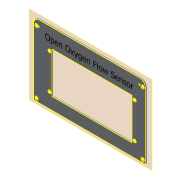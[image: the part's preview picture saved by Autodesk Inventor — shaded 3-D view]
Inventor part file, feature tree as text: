
AUTODESK INVENTOR PART (.ipt)
format: ipt  version: 2019.4 (Build 234330000, 330)  size: 126,976 bytes
history: native  units: mm
features: sketch x2, other x2, plane x1, extrude x1, fillet x1, reference x1, projected_geometry x1
ambient origin geometry x8: Origin, YZ Plane, XZ Plane, XY Plane, X Axis, Y Axis, Z Axis, Center Point
bodies: Solid1 (feature_tree)
feature tree (9):
  plane  "Work Plane1"
  extrude  "Extrusion1"  Depth=36.0mm
  fillet  "Fillet1"  Radius=74.5mm
  sketch  "Sketch2"  dims[d3=31.0mm d4=2.8mm d5=2.8mm d6=2.8mm d7=2.8mm d8=1.0mm d9=0.0mm d10=5.0mm]
  sketch  "Sketch1"  dims[d0=70.0mm d1=36.0mm d2=74.5mm]
  reference  "Reference1"
  projected_geometry  "Projected Loop1"
  other  "Assemlby_OpenOxygen.iam"
  other  "03_OpenOxygen_Box:1"
